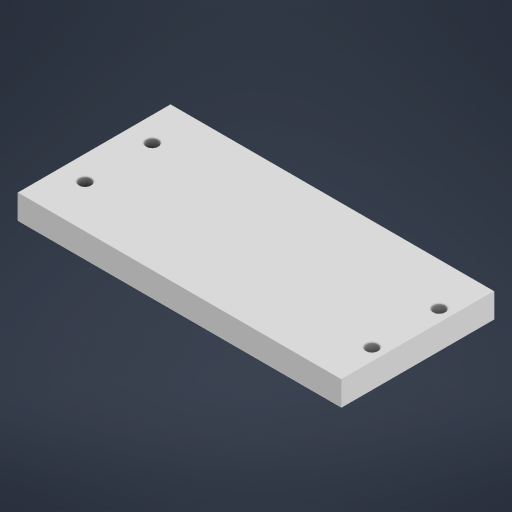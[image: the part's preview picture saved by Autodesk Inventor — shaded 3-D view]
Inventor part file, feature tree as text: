
AUTODESK INVENTOR PART (.ipt)
format: ipt  version: 2023.2 (Build 272271000, 271)  size: 202,752 bytes
history: native  units: mm
features: sketch x1
ambient origin geometry x8: Origin, YZ Plane, XZ Plane, XY Plane, X Axis, Y Axis, Z Axis, Center Point
bodies: Body1 (feature_tree)
feature tree (1):
  sketch  "Sketch1"  dims[d228=25.0mm d229=53.0mm d232=11.0mm d233=4.0mm d234=2.0mm d238=4.0mm d239=0.0mm d240=2.0mm d9=0.5mm d10=0.872665mm d11=0.5mm d12=0.872665mm d13=0.5mm d14=0.872665mm d27=0.5mm d28=0.872665mm d29=0.5mm d30=0.872665mm d88=0.5mm d89=0.872665mm d90=0.5mm d91=0.872665mm d116=0.5mm d117=0.872665mm d118=0.5mm d119=0.872665mm d154=0.5mm d155=0.872665mm d156=0.5mm d157=0.872665mm d181=0.5mm d182=0.872665mm d183=0.5mm d184=0.872665mm d221=0.5mm d222=0.872665mm d223=0.5mm d224=0.872665mm]
